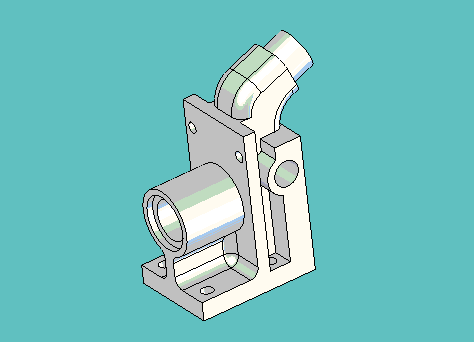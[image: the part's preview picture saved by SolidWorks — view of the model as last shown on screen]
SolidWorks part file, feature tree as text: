
SOLIDWORKS PART (.sldprt)
format: sldprt  version: not decoded by parser v0  size: 1,624,064 bytes
history: native  units: mm
features: sketch x21, boolean_combine x9, cut_extrude x9, extrude x8, fillet x3, revolve x2, material x1, chamfer x1, sweep x1 (+11 scaffold rows collapsed)
feature tree (66):
  scaffold x11  (default folders/planes/origin — collapsed)
  material  "Material <not specified>"
  sketch  "Sketch1"  dims[D1=4.7498mm D2=11.43mm D3=11.43mm D4=30.9626mm]
  extrude  "Extrude1"  Depth=41.275mm
  sketch  "Sketch5"  dims[D1=5.6515mm D2=5.6515mm D3=14.097mm]
  extrude  "Extrude7"  Depth=4.7752mm
  boolean_combine  "Combine4"
  sketch  "Sketch6"  dims[D2=7.0358mm D1=20.6502mm]
  extrude  "Extrude8"  Depth=38.1mm
  boolean_combine  "Combine5"
  sketch  "Sketch7"  dims[D1=10.16mm]
  extrude  "Extrude10"  Depth=22.2758mm
  boolean_combine  "Combine6"
  sketch  "Sketch8"  dims[D1=6.604mm D2=4.7752mm]
  extrude  "Extrude11"  Depth=17.4498mm
  boolean_combine  "Combine7"
  sketch  "Sketch9"  dims[c1.D3=6.5278mm c1.D1=28.956mm c1.D2=4.7625mm c2.D1=27.1272mm]
  extrude  "Extrude12"  Depth=38.1mm
  boolean_combine  "Combine8"
  sketch  "Sketch11"  dims[c1.D1=0.381mm c1.D2=3.175mm c2.D1=3.175mm c2.D3=0.254mm c2.D4=7.62mm c2.D2=0.381mm]
  revolve  "Revolve2"  Angle=360deg
  boolean_combine  "Combine11"
  sketch  "Sketch12"  dims[c1.D1=3.175mm c1.D2=3.175mm c1.D3=3.175mm c1.D7=3.175mm c1.D4=9.525mm c1.D5=7.9248mm c1.D6=7.9248mm c2.D7=26.9748mm c2.D8=26.9748mm c2.D4=26.9875mm c2.D3=7.9248mm c2.D6=9.525mm c2.D5=7.9248mm c3.D8=7.9248mm c3.D9=9.525mm c4.D8=7.9248mm]
  extrude  "Extrude14"  Depth=12.7mm
  boolean_combine  "Combine12"
  chamfer  "Chamfer1"  Distance=0.889mm Angle=15deg
  sketch  "Sketch21"  dims[D1=3.175mm D2=15.875mm]
  cut_extrude  "Cut-Extrude6"  [1 undecoded]
  sketch  "Sketch24"  dims[c1.D2=2.032mm c1.D3=~2.38125mm c1.D4=~2.38125mm c1.D5=3.175mm c1.D1=4.7625mm c2.D3=3.175mm c2.D4=1.5875mm c2.D5=1.5875mm c2.D1=0.0mm]
  cut_extrude  "Cut-Extrude9"  [1 undecoded]
  fillet  "Fillet1"  Radius=2.38125mm
  sketch  "Sketch25"  dims[c1.D2=6.5278mm c1.D1=3.175mm c2.D2=22.225mm c2.D3=6.35mm c3.D2=1.778mm c3.D4=3.175mm c3.D5=7.9375mm c4.D4=31.75mm]
  cut_extrude  "Cut-Extrude10"  Depth=5.55625mm
  sketch  "Sketch26"  dims[D1=0.0mm]
  cut_extrude  "Cut-Extrude11"  Depth=5.55625mm
  sketch  "Sketch27"  dims[D3=2.7051mm D5=2.7051mm D1=34.925mm D2=8.89mm D4=8.89mm]
  cut_extrude  "Cut-Extrude12"  [1 undecoded]
  sketch  "Sketch29"  dims[D1=0.0mm]
  cut_extrude  "Cut-Extrude14"  Depth=6.35mm
  sketch  "Sketch30"
  sketch  "Sketch31"  dims[c1.D1=~20.20113mm c2.D1=70.0deg c2.D2=12.7mm c2.D3=6.35mm c2.D4=4.953mm c2.D5=4.953mm]
  sweep  "Sweep1"
  sketch  "Sketch32"  dims[c1.D1=9.525mm c1.D4=5.08mm c1.D3=6.35mm c2.D1=~7.666823mm c3.D1=54.0deg c3.D2=~15.09935mm c4.D2=42.0deg c4.D1=5.08mm c5.D2=5.08mm c5.D3=6.35mm c5.D1=~5.87502mm c6.D2=~5.87502mm]
  extrude  "Extrude15"  [1 undecoded]
  boolean_combine  "Combine13"
  boolean_combine  "Combine14"
  sketch  "Sketch33"  dims[D1=7.1628mm]
  cut_extrude  "Cut-Extrude15"  Depth=6.35mm
  sketch  "Sketch34"  dims[D2=10.414mm D3=3.175mm D4=3.175mm D1=0.0mm]
  cut_extrude  "Cut-Extrude16"  Depth=6.35mm
  fillet  "Fillet2"  Radius=3.175mm
  fillet  "Fillet3"  Radius=0.79375mm
  sketch  "Sketch35"  dims[c1.D1=20.6502mm c1.D2=0.508mm c1.D3=3.4022mm c1.D4=7.366mm c1.D5=~0.736288mm c2.D5=15.0deg c2.D6=0.7112mm c2.D7=~2.324864mm c3.D7=~72.187055deg c4.D7=~1.885774mm]
  revolve  "Revolve3"  Angle=360deg
  sketch  "Sketch37"  dims[D1=13.5128mm]
  cut_extrude  "Cut-Extrude18"  Depth=1.5875mm
decode coverage: 39 of 54 modeling features carry decoded parameters
note: ~ marks probable driven/reference dimensions
note: 4 parameter values undecoded
summary: no parameter record found for 4 features
note: suppression state not decoded; provenance and decode notes live in map.json
